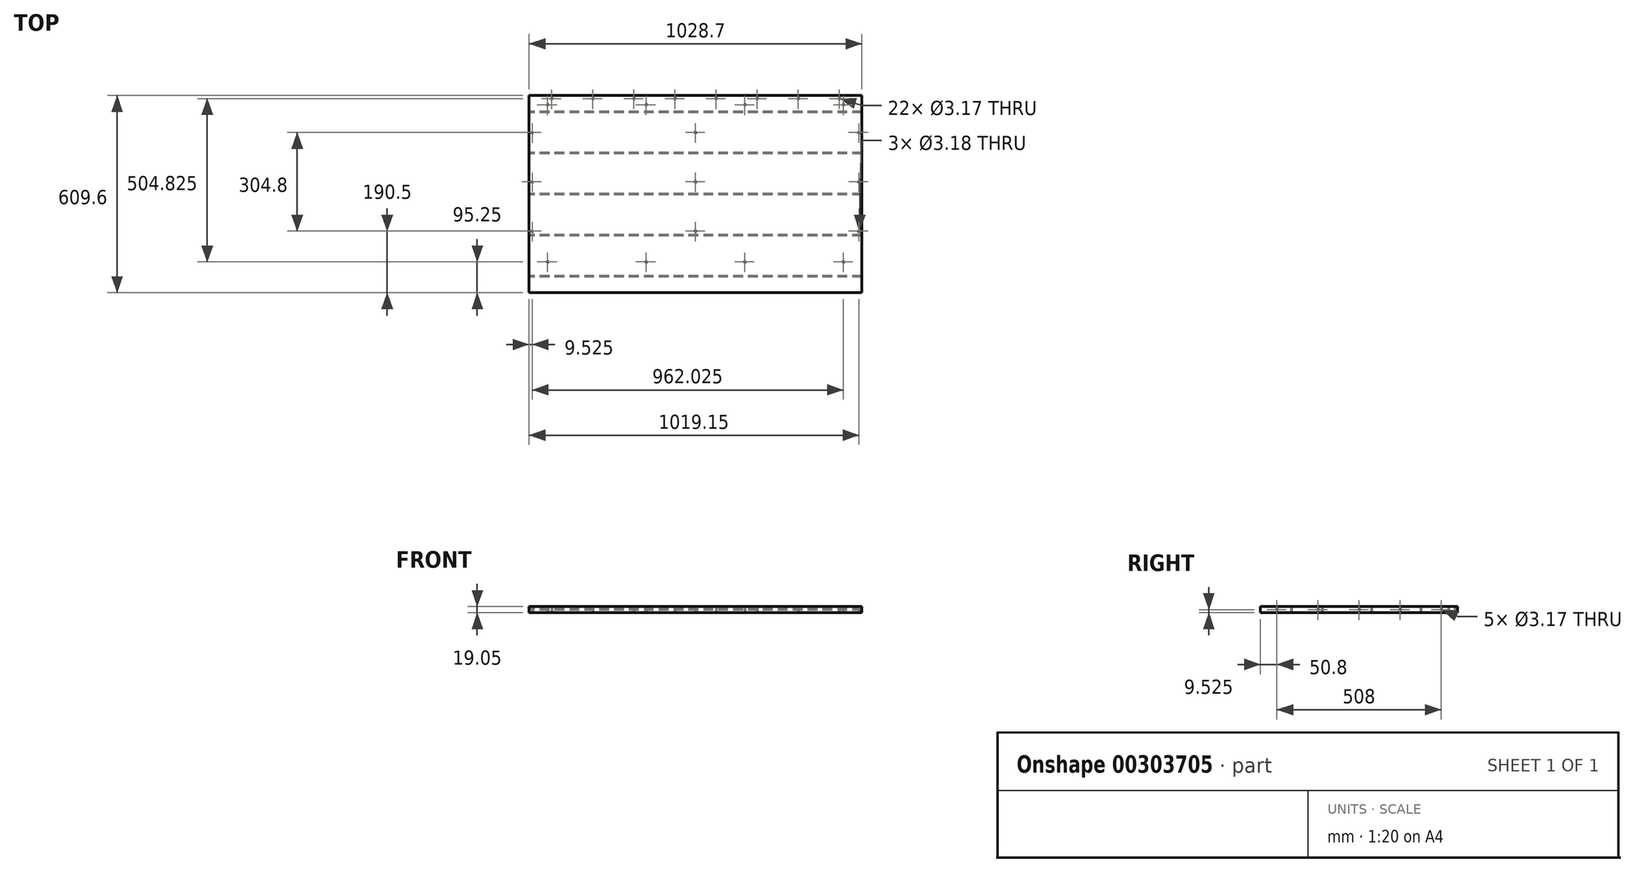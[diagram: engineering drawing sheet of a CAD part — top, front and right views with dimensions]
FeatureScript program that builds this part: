
annotation { "Feature Type Name" : "Feature", "Feature Type Description" : "" }
export const myFeature = defineFeature(function(context is Context, id is Id, definition is map)
    precondition{}
    {
        {
            var Q0;
            Q0=qCreatedBy(makeId("Front.planeOp"),FACE);
            var sketch = newSketch(context, id + "F0", { "sketchPlane" : qUnion([Q0])});
            skLineSegment(sketch, "E0.bottom", {"start": v(0, 0) * mm, "end": v(1028.7, 0) * mm});
            skLineSegment(sketch, "E0.top", {"start": v(0, 19.05) * mm, "end": v(1028.7, 19.05) * mm});
            skLineSegment(sketch, "E0.left", {"start": v(0, 0) * mm, "end": v(0, 19.05) * mm});
            skLineSegment(sketch, "E0.right", {"start": v(1028.7, 0) * mm, "end": v(1028.7, 19.05) * mm});
            skSolve(sketch);
        }
        {
            var Q0;
            Q0 = qSketchRegion(id + "F0", true);
            extrude(context, id + "F1", {"entities" : qUnion([Q0]), "oppositeDirection" : true, "depth" : 609.6 * mm});
        }
        {
            var Q0;
            Q0=qCreatedBy(makeId("Top.planeOp"),FACE);
            var sketch = newSketch(context, id + "F2", { "sketchPlane" : qUnion([Q0])});
            skCircle(sketch, "E1", {"center": v(9.53, 495.3) * mm, "radius": 1.59 * mm});
            skCircle(sketch, "E2.0.1.0", {"center": v(9.53, 342.9) * mm, "radius": 1.59 * mm});
            skCircle(sketch, "E2.0.2.0", {"center": v(9.53, 190.5) * mm, "radius": 1.59 * mm});
            skCircle(sketch, "E2.1.0.0", {"center": v(514.34, 495.3) * mm, "radius": 1.59 * mm});
            skCircle(sketch, "E2.1.1.0", {"center": v(514.34, 342.9) * mm, "radius": 1.59 * mm});
            skCircle(sketch, "E2.1.2.0", {"center": v(514.34, 190.5) * mm, "radius": 1.59 * mm});
            skCircle(sketch, "E2.2.0.0", {"center": v(1019.15, 495.3) * mm, "radius": 1.59 * mm});
            skCircle(sketch, "E2.2.1.0", {"center": v(1019.15, 342.9) * mm, "radius": 1.59 * mm});
            skCircle(sketch, "E2.2.2.0", {"center": v(1019.15, 190.5) * mm, "radius": 1.59 * mm});
            skLineSegment(sketch, "E2.direction1", {"start": v(9.53, 495.3) * mm, "end": v(514.34, 495.3) * mm, "construction": true});
            skLineSegment(sketch, "E2.direction2", {"start": v(9.53, 495.3) * mm, "end": v(9.53, 342.9) * mm, "construction": true});
            skSolve(sketch);
        }
        {
            var Q0;
            Q0 = qSketchRegion(id + "F2", true);
            extrude(context, id + "F3", {"entities" : qUnion([Q0]), "operationType" : NewBodyOperationType.REMOVE, "endBound" : BoundingType.THROUGH_ALL, "depth" : 25.4 * mm});
        }
        {
            var Q0;
            Q0=qCreatedBy(makeId("Top.planeOp"),FACE);
            var sketch = newSketch(context, id + "F4", { "sketchPlane" : qUnion([Q0])});
            skCircle(sketch, "E3", {"center": v(57.15, 581.02) * mm, "radius": 1.59 * mm});
            skCircle(sketch, "E4.0.1.0", {"center": v(57.15, 95.25) * mm, "radius": 1.59 * mm});
            skCircle(sketch, "E4.1.0.0", {"center": v(361.95, 581.02) * mm, "radius": 1.59 * mm});
            skCircle(sketch, "E4.1.1.0", {"center": v(361.95, 95.25) * mm, "radius": 1.59 * mm});
            skCircle(sketch, "E4.2.0.0", {"center": v(666.75, 581.02) * mm, "radius": 1.59 * mm});
            skCircle(sketch, "E4.2.1.0", {"center": v(666.75, 95.25) * mm, "radius": 1.59 * mm});
            skCircle(sketch, "E4.3.0.0", {"center": v(971.55, 581.02) * mm, "radius": 1.59 * mm});
            skCircle(sketch, "E4.3.1.0", {"center": v(971.55, 95.25) * mm, "radius": 1.59 * mm});
            skLineSegment(sketch, "E4.direction1", {"start": v(57.15, 581.02) * mm, "end": v(361.95, 581.02) * mm, "construction": true});
            skLineSegment(sketch, "E4.direction2", {"start": v(57.15, 581.02) * mm, "end": v(57.15, 95.25) * mm, "construction": true});
            skSolve(sketch);
        }
        {
            var Q0;
            Q0=qCreatedBy(makeId("Right.planeOp"),FACE);
            var sketch = newSketch(context, id + "F5", { "sketchPlane" : qUnion([Q0])});
            skCircle(sketch, "E5", {"center": v(50.8, 9.53) * mm, "radius": 1.59 * mm});
            skCircle(sketch, "E6.1.0.0", {"center": v(177.8, 9.53) * mm, "radius": 1.59 * mm});
            skCircle(sketch, "E6.2.0.0", {"center": v(304.8, 9.53) * mm, "radius": 1.59 * mm});
            skCircle(sketch, "E6.3.0.0", {"center": v(431.8, 9.53) * mm, "radius": 1.59 * mm});
            skCircle(sketch, "E6.4.0.0", {"center": v(558.8, 9.53) * mm, "radius": 1.59 * mm});
            skLineSegment(sketch, "E6.direction1", {"start": v(50.8, 9.53) * mm, "end": v(177.8, 9.53) * mm, "construction": true});
            skSolve(sketch);
        }
        {
            var Q0;
            Q0 = qSketchRegion(id + "F5", true);
            extrude(context, id + "F6", {"entities" : qUnion([Q0]), "operationType" : NewBodyOperationType.REMOVE, "endBound" : BoundingType.THROUGH_ALL, "depth" : 25.4 * mm});
        }
        {
            var Q0;
            Q0 = qSketchRegion(id + "F4", true);
            extrude(context, id + "F7", {"entities" : qUnion([Q0]), "operationType" : NewBodyOperationType.REMOVE, "endBound" : BoundingType.THROUGH_ALL, "depth" : 25.4 * mm});
        }
        {
            var Q0;
            Q0=qCreatedBy(makeId("Top.planeOp"),FACE);
            var sketch = newSketch(context, id + "F8", { "sketchPlane" : qUnion([Q0])});
            skCircle(sketch, "E7", {"center": v(69.85, 600.08) * mm, "radius": 1.59 * mm});
            skCircle(sketch, "E8.1.0.0", {"center": v(196.85, 600.08) * mm, "radius": 1.59 * mm});
            skCircle(sketch, "E8.2.0.0", {"center": v(323.85, 600.08) * mm, "radius": 1.59 * mm});
            skCircle(sketch, "E8.3.0.0", {"center": v(450.85, 600.08) * mm, "radius": 1.59 * mm});
            skCircle(sketch, "E8.4.0.0", {"center": v(577.85, 600.08) * mm, "radius": 1.59 * mm});
            skCircle(sketch, "E8.5.0.0", {"center": v(704.85, 600.08) * mm, "radius": 1.59 * mm});
            skCircle(sketch, "E8.6.0.0", {"center": v(831.85, 600.08) * mm, "radius": 1.59 * mm});
            skCircle(sketch, "E8.7.0.0", {"center": v(958.85, 600.08) * mm, "radius": 1.59 * mm});
            skLineSegment(sketch, "E8.direction1", {"start": v(69.85, 600.08) * mm, "end": v(196.85, 600.08) * mm, "construction": true});
            skSolve(sketch);
        }
        {
            var Q0;
            Q0 = qSketchRegion(id + "F8", true);
            extrude(context, id + "F9", {"entities" : qUnion([Q0]), "operationType" : NewBodyOperationType.REMOVE, "endBound" : BoundingType.THROUGH_ALL, "depth" : 25.4 * mm});
        }
    });
